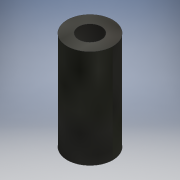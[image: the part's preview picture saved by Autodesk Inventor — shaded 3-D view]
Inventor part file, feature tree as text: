
AUTODESK INVENTOR PART (.ipt)
format: ipt  version: 2020.2 (Build 242310000, 310)  size: 96,768 bytes
history: native  units: mm
features: other x1, extrude x1, sketch x1
ambient origin geometry x8: Origin, YZ Plane, XZ Plane, XY Plane, X Axis, Y Axis, Z Axis, Center Point
bodies: Body1 (feature_tree)
feature tree (3):
  other  "ソリッド1"
  extrude  "押し出し1"  Depth=6.0mm
  sketch  "スケッチ1"
